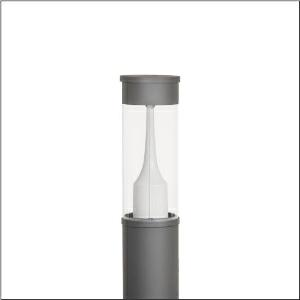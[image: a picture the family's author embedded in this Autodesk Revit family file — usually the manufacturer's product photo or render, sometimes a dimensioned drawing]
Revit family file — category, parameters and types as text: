
# Revit family: city-light_120_iq___p1_0a_5xa5285bf14h_8c15
name_source: partatom
category: Lighting Fixtures
units: mm (PartAtom-declared; Revit-internal decimal feet)

## family parameters
Cut with Voids When Loaded = No
Host = Face
Light Source = No
Part Type = Normal
Room Calculation Point = No
Round Connector Dimension = Use Diameter
Shared = No

## types (1)
- --- (1 x LED, 1510 lm, 12.9 W, 2200K)
    Apparent Load = 13 VA
    CIE Flux Codes = 32 61 90 93 100
    Color Rendering = 70
    Color Temperature = 2200K
    Default Elevation = 1800 mm
    Description = City-Light 120 iQ, bollard luminaire, Module 540 iQ-SR, primary light control with 3 zone facetted reflector, of plastic, silver coated, highly specular, structured, primary optical cover: cover, of PMMA, transparent, partly coated, light distribution: P1.0a, primary light characteristic: strongly asymmetric, LED, High Power LED, rated luminous flux: 1.510lm, luminous efficacy: 117lm/W, light colour: 722, colour temperature: 2200K, control gear: ECG iQ, control: presetting dimming logarithmic, Street-Remote, Auto-Match, Temp-Guard, Lumen-Switch, Night-Set, Smart-Wire, Light-Fading, Desk-Remote (wireless, voltage-free reading and setting of iQ features in the workshop via application-optimized NFC function/RFID function), optimised constant luminous flux control (CLO 2.0), with terminal, 6-pole, max. 2.5mm², mains connection: 230..240V, AC, 50/60Hz, start of lifetime: 13W, end of service life: 13W, reduction: 6W, luminaire housing, cylindrical, of extruded aluminium section, coated, Siteco® metallic grey (DB 702S), length: 1.200mm, diameter: 200mm, Module 540 iQ-SR, traffic white (RAL 9016), equipment: standard, protection rating (complete): IP54, insulation class (complete): insulation class II (safety insulation), certification: CE, ENEC, VDE, packaging unit: 1 piece

Light Distribution: P1.0a
    Height = 500 mm
    Lamp = 1 x LED
    Lamp Light Flux = 1510 lm
    Lamp Power = 12.9 W
    Lamp count = 1
    Length = 200 mm  [stored 0.656168 ft]
    Luminous efficacy = 117 lm/W
    Manufacturer = Siteco
    ModVariant = No
    Model = 5XA5285BF14H
    Mounting Place = Floor
    Mounting Type = Freestanding
    Number of Poles = 1
    OnlyDefault = Yes
    Power Factor = 1
    Product Name = City-Light 120 iQ | P1.0a
    Product group = bollard luminaire
    ProductGroupID = 1304
    Protection Class = Protection class II
    Protection Degree = IP 54
    RLX_Detail_Level = 1
    RLX_Emergency_Light_Flux = 0 lm
    RLX_Emergency_Type = 0
    RLX_Emergency_Type_DB = No
    RlxData = <blob elided: 53061 chars, md5=5d786156>
    Socket = socket
    Standby Power = 0 W
    System Light Flux = 1510 lm
    System Power = 13 W
    Type Comments = factory setting: luminous flux: 100 % | dim-lin: 254 | 516 mA
    Type Image = l_1006922.jpg
    URL = http://relux.com
    VarID = @adj_109803
    Voltage = 0 V
    Weight = 0.00 kg
    Width = 0 mm  [stored 0 ft]

note: [stored X ft] marks values corroborated as IEEE doubles in the binary element streams (Revit-internal decimal feet)

## geometry (parser evidence)
native form markers: Blend x4, Sweep x10
no freeform markers — native parametric forms only
